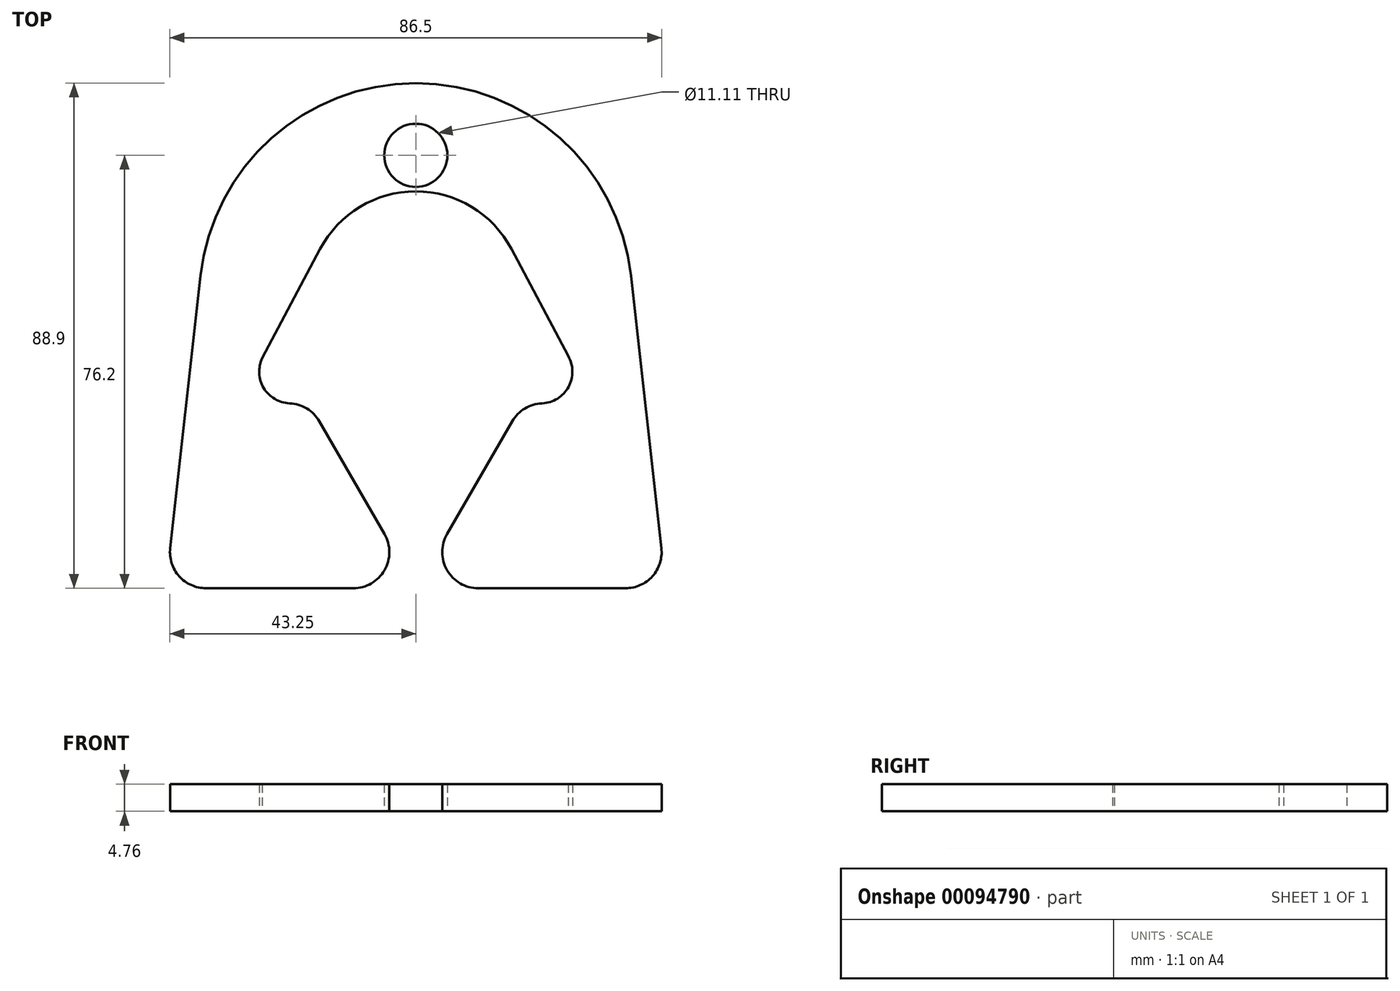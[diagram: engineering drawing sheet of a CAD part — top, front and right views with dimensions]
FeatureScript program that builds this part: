
annotation { "Feature Type Name" : "Feature", "Feature Type Description" : "" }
export const myFeature = defineFeature(function(context is Context, id is Id, definition is map)
    precondition{}
    {
        {
            var Q0;
            Q0=qCreatedBy(makeId("Top.planeOp"),FACE);
            var sketch = newSketch(context, id + "F0", { "sketchPlane" : qUnion([Q0])});
            skArc(sketch, "E0", {"start": v(37.87, 4.22) * mm, "mid": v(0, 38.1) * mm, "end": v(-37.87, 4.22) * mm});
            skCircle(sketch, "E1", {"center": v(0, 25.4) * mm, "radius": 5.56 * mm});
            skArc(sketch, "E2.1.0", {"start": v(-27, -10.28) * mm, "mid": v(-26.76, -15.56) * mm, "end": v(-22.21, -18.25) * mm});
            skArc(sketch, "E2.2.0", {"start": v(22.21, -18.25) * mm, "mid": v(26.86, -15.39) * mm, "end": v(26.81, -9.93) * mm});
            skArc(sketch, "E3", {"start": v(16.84, 8.91) * mm, "mid": v(0, 19.05) * mm, "end": v(-16.84, 8.91) * mm});
            skLineSegment(sketch, "E4.top", {"start": v(-11, -50.8) * mm, "end": v(-36.9, -50.8) * mm});
            skLineSegment(sketch, "E5.top", {"start": v(11, -50.8) * mm, "end": v(36.9, -50.8) * mm});
            skLineSegment(sketch, "E6", {"start": v(-43.2, -43.75) * mm, "end": v(-37.87, 4.22) * mm});
            skPoint(sketch, "E4.right.start.orphan", {"position": v(-44, 25.4) * mm});
            skLineSegment(sketch, "E7", {"start": v(43.2, -43.75) * mm, "end": v(37.87, 4.22) * mm});
            skPoint(sketch, "E5.right.start.orphan", {"position": v(44, 25.4) * mm});
            skLineSegment(sketch, "E8", {"start": v(-16.96, -21.42) * mm, "end": v(-5.5, -41.27) * mm});
            skLineSegment(sketch, "E9", {"start": v(5.5, -41.28) * mm, "end": v(16.96, -21.42) * mm});
            skPoint(sketch, "E10.visualSharp", {"position": v(0, -50.8) * mm});
            skArc(sketch, "E10.filletArc", {"start": v(-11, -50.8) * mm, "mid": v(-5.5, -47.62) * mm, "end": v(-5.5, -41.27) * mm});
            skArc(sketch, "E11.filletArc", {"start": v(5.5, -41.28) * mm, "mid": v(5.5, -47.63) * mm, "end": v(11, -50.8) * mm});
            skPoint(sketch, "E12.visualSharp", {"position": v(-44, -50.8) * mm});
            skArc(sketch, "E12.filletArc", {"start": v(-43.2, -43.75) * mm, "mid": v(-41.63, -48.68) * mm, "end": v(-36.9, -50.8) * mm});
            skPoint(sketch, "E13.visualSharp", {"position": v(44, -50.8) * mm});
            skArc(sketch, "E13.filletArc", {"start": v(36.9, -50.8) * mm, "mid": v(41.63, -48.68) * mm, "end": v(43.2, -43.75) * mm});
            skLineSegment(sketch, "E14", {"start": v(-27, -10.28) * mm, "end": v(-16.84, 8.91) * mm});
            skLineSegment(sketch, "E15.MirrorCS", {"start": v(27, -10.28) * mm, "end": v(16.84, 8.91) * mm});
            skPoint(sketch, "E16.visualSharp", {"position": v(-19.22, -17.51) * mm});
            skArc(sketch, "E16.filletArc", {"start": v(-16.96, -21.42) * mm, "mid": v(-19.18, -19.16) * mm, "end": v(-22.21, -18.25) * mm});
            skPoint(sketch, "E17.visualSharp", {"position": v(19.22, -17.51) * mm});
            skArc(sketch, "E17.filletArc", {"start": v(22.21, -18.25) * mm, "mid": v(19.18, -19.16) * mm, "end": v(16.96, -21.42) * mm});
            skSolve(sketch);
        }
        {
            var Q0;
            Q0=makeQuery(id+"F0.imprint","IMPRINT",FACE,{"disambiguationData":[TD([[makeQuery(id+"F0.imprint","IMPRINT",EDGE,{"derivedFrom":sQuery(id+"F0.wireOp",EDGE,"E1")}),-1.0]])]});
            extrude(context, id + "F1", {"entities" : qUnion([Q0]), "depth" : 4.76 * mm});
        }
    });
